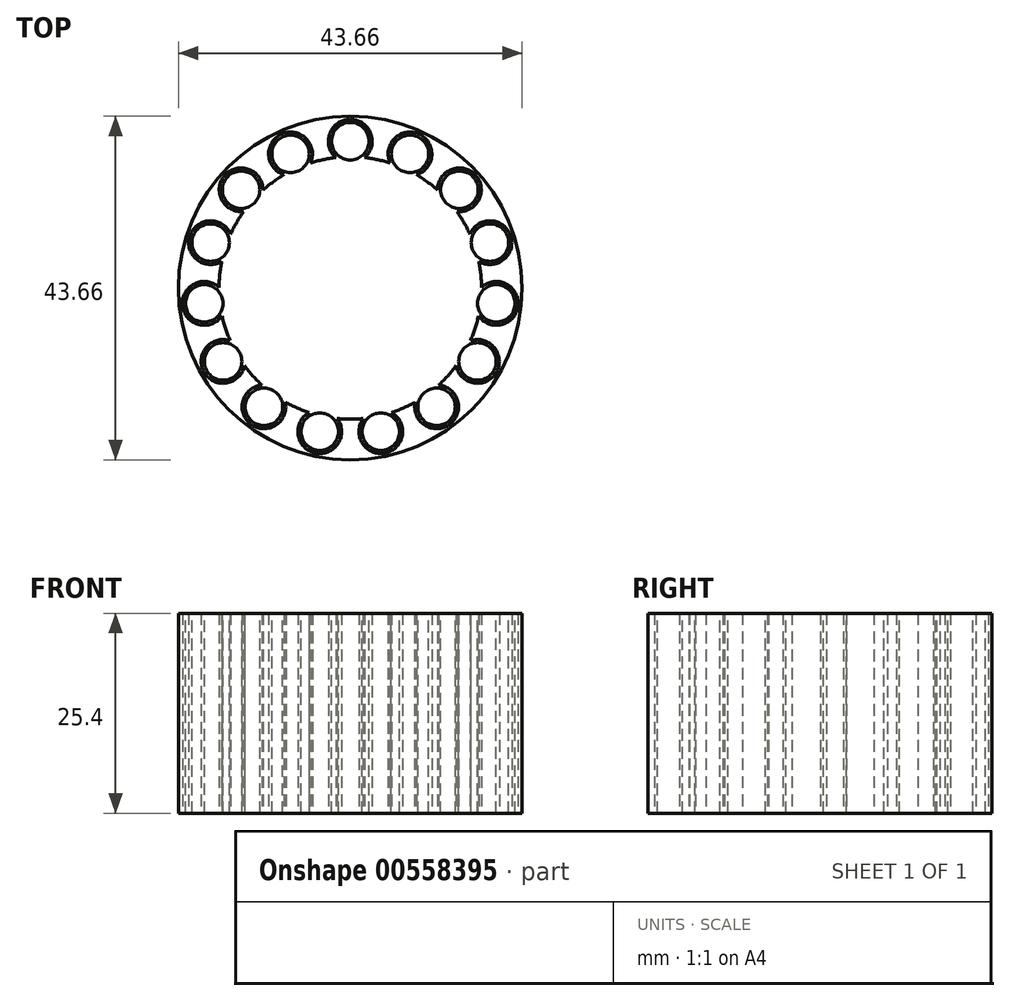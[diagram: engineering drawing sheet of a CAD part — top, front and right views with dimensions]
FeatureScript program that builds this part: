
annotation { "Feature Type Name" : "Feature", "Feature Type Description" : "" }
export const myFeature = defineFeature(function(context is Context, id is Id, definition is map)
    precondition{}
    {
        {
            var Q0;
            Q0=qCreatedBy(makeId("Top.planeOp"),FACE);
            var sketch = newSketch(context, id + "F0", { "sketchPlane" : qUnion([Q0])});
            skCircle(sketch, "E0", {"center": v(0, 0) * mm, "radius": 21.83 * mm});
            skCircle(sketch, "E1", {"center": v(0, 18.65) * mm, "radius": 2.78 * mm});
            skCircle(sketch, "E2.1.0", {"center": v(-7.59, 17.04) * mm, "radius": 2.78 * mm});
            skCircle(sketch, "E2.2.0", {"center": v(-13.86, 12.48) * mm, "radius": 2.78 * mm});
            skCircle(sketch, "E2.3.0", {"center": v(-17.74, 5.76) * mm, "radius": 2.78 * mm});
            skCircle(sketch, "E2.4.0", {"center": v(-18.55, -1.95) * mm, "radius": 2.78 * mm});
            skCircle(sketch, "E2.5.0", {"center": v(-16.15, -9.33) * mm, "radius": 2.78 * mm});
            skCircle(sketch, "E2.6.0", {"center": v(-10.96, -15.1) * mm, "radius": 2.78 * mm});
            skCircle(sketch, "E2.7.0", {"center": v(-3.88, -18.25) * mm, "radius": 2.78 * mm});
            skCircle(sketch, "E2.8.0", {"center": v(3.88, -18.25) * mm, "radius": 2.78 * mm});
            skCircle(sketch, "E2.9.0", {"center": v(10.96, -15.1) * mm, "radius": 2.78 * mm});
            skCircle(sketch, "E2.10.0", {"center": v(16.15, -9.33) * mm, "radius": 2.78 * mm});
            skCircle(sketch, "E2.11.0", {"center": v(18.55, -1.95) * mm, "radius": 2.78 * mm});
            skCircle(sketch, "E3.1.12.0", {"center": v(17.74, 5.76) * mm, "radius": 2.78 * mm});
            skCircle(sketch, "E3.1.13.0", {"center": v(13.86, 12.48) * mm, "radius": 2.78 * mm});
            skCircle(sketch, "E3.1.14.0", {"center": v(7.59, 17.04) * mm, "radius": 2.78 * mm});
            skCircle(sketch, "E4", {"center": v(0, 0) * mm, "radius": 16.67 * mm});
            skSolve(sketch);
        }
        {
            var Q0;
            Q0 = qSketchRegion(id + "F0", true);
            extrude(context, id + "F1", {"entities" : qUnion([Q0]), "depth" : 25.4 * mm, "offsetDistance" : 25.4 * mm});
        }
        {
            var Q0;
            Q0=makeQuery(id+"F1.opExtrude","CAP_FACE",FACE,{"disambiguationData":[OSD([sQuery(id+"F0.wireOp",EDGE,"E0"),sQuery(id+"F0.wireOp",EDGE,"E1"),sQuery(id+"F0.wireOp",EDGE,"E2.1.0"),sQuery(id+"F0.wireOp",EDGE,"E2.2.0"),sQuery(id+"F0.wireOp",EDGE,"E2.3.0"),sQuery(id+"F0.wireOp",EDGE,"E2.4.0"),sQuery(id+"F0.wireOp",EDGE,"E2.5.0"),sQuery(id+"F0.wireOp",EDGE,"E2.6.0"),sQuery(id+"F0.wireOp",EDGE,"E2.7.0"),sQuery(id+"F0.wireOp",EDGE,"E2.8.0"),sQuery(id+"F0.wireOp",EDGE,"E2.9.0"),sQuery(id+"F0.wireOp",EDGE,"E2.10.0"),sQuery(id+"F0.wireOp",EDGE,"E2.11.0"),sQuery(id+"F0.wireOp",EDGE,"E3.1.12.0"),sQuery(id+"F0.wireOp",EDGE,"E3.1.13.0"),sQuery(id+"F0.wireOp",EDGE,"E3.1.14.0"),sQuery(id+"F0.wireOp",EDGE,"E4")])],"isStart":true});
            var sketch = newSketch(context, id + "F2", { "sketchPlane" : qUnion([Q0])});
            skCircle(sketch, "E5", {"center": v(0, 0) * mm, "radius": 20.76 * mm});
            skCircle(sketch, "E6", {"center": v(0, 0) * mm, "radius": 20.3 * mm});
            skSolve(sketch);
        }
        {
            var Q0;
            Q0 = qSketchRegion(id + "F2", true);
            extrude(context, id + "F3", {"entities" : qUnion([Q0]), "operationType" : NewBodyOperationType.ADD, "oppositeDirection" : true, "depth" : 0.03 * mm, "offsetDistance" : 25.4 * mm});
        }
        {
            var Q0;
            Q0=makeQuery(id+"F1.opExtrude","CAP_FACE",FACE,{"disambiguationData":[OSD([sQuery(id+"F0.wireOp",EDGE,"E0"),sQuery(id+"F0.wireOp",EDGE,"ILeCSpun-wmdF-93Xr-9eFY-KsnJDnbWFszn"),sQuery(id+"F0.wireOp",EDGE,"E1"),sQuery(id+"F0.wireOp",EDGE,"E2.1.0"),sQuery(id+"F0.wireOp",EDGE,"E2.2.0"),sQuery(id+"F0.wireOp",EDGE,"E2.3.0"),sQuery(id+"F0.wireOp",EDGE,"E2.4.0"),sQuery(id+"F0.wireOp",EDGE,"E2.5.0"),sQuery(id+"F0.wireOp",EDGE,"E2.6.0"),sQuery(id+"F0.wireOp",EDGE,"E2.7.0"),sQuery(id+"F0.wireOp",EDGE,"E2.8.0"),sQuery(id+"F0.wireOp",EDGE,"E2.9.0"),sQuery(id+"F0.wireOp",EDGE,"E2.10.0"),sQuery(id+"F0.wireOp",EDGE,"E2.11.0"),sQuery(id+"F0.wireOp",EDGE,"E3.1.12.0"),sQuery(id+"F0.wireOp",EDGE,"E3.1.13.0"),sQuery(id+"F0.wireOp",EDGE,"E3.1.14.0")])],"isStart":false});
            var sketch = newSketch(context, id + "F4", { "sketchPlane" : qUnion([Q0])});
            skCircle(sketch, "E7", {"center": v(0, 18.65) * mm, "radius": 2.38 * mm});
            skCircle(sketch, "E8.1.0", {"center": v(-7.59, 17.04) * mm, "radius": 2.38 * mm});
            skCircle(sketch, "E8.2.0", {"center": v(-13.86, 12.48) * mm, "radius": 2.38 * mm});
            skPoint(sketch, "E8.center", {"position": v(0, 0) * mm});
            skCircle(sketch, "E9.1.3.0", {"center": v(-17.74, 5.76) * mm, "radius": 2.38 * mm});
            skCircle(sketch, "E9.1.4.0", {"center": v(-18.55, -1.95) * mm, "radius": 2.38 * mm});
            skCircle(sketch, "E9.1.5.0", {"center": v(-16.15, -9.33) * mm, "radius": 2.38 * mm});
            skCircle(sketch, "E9.1.6.0", {"center": v(-10.96, -15.1) * mm, "radius": 2.38 * mm});
            skCircle(sketch, "E9.1.7.0", {"center": v(-3.88, -18.25) * mm, "radius": 2.38 * mm});
            skCircle(sketch, "E9.1.8.0", {"center": v(3.88, -18.25) * mm, "radius": 2.38 * mm});
            skCircle(sketch, "E9.1.9.0", {"center": v(10.96, -15.1) * mm, "radius": 2.38 * mm});
            skCircle(sketch, "E9.1.10.0", {"center": v(16.15, -9.33) * mm, "radius": 2.38 * mm});
            skCircle(sketch, "E9.1.11.0", {"center": v(18.55, -1.95) * mm, "radius": 2.38 * mm});
            skCircle(sketch, "E9.1.12.0", {"center": v(17.74, 5.76) * mm, "radius": 2.38 * mm});
            skCircle(sketch, "E9.1.13.0", {"center": v(13.86, 12.48) * mm, "radius": 2.38 * mm});
            skCircle(sketch, "E9.1.14.0", {"center": v(7.59, 17.04) * mm, "radius": 2.38 * mm});
            skSolve(sketch);
        }
        {
            var Q0;
            Q0 = qSketchRegion(id + "F4", true);
            extrude(context, id + "F5", {"entities" : qUnion([Q0]), "operationType" : NewBodyOperationType.ADD, "oppositeDirection" : true, "depth" : 25.4 * mm, "offsetDistance" : 25.4 * mm});
        }
    });
